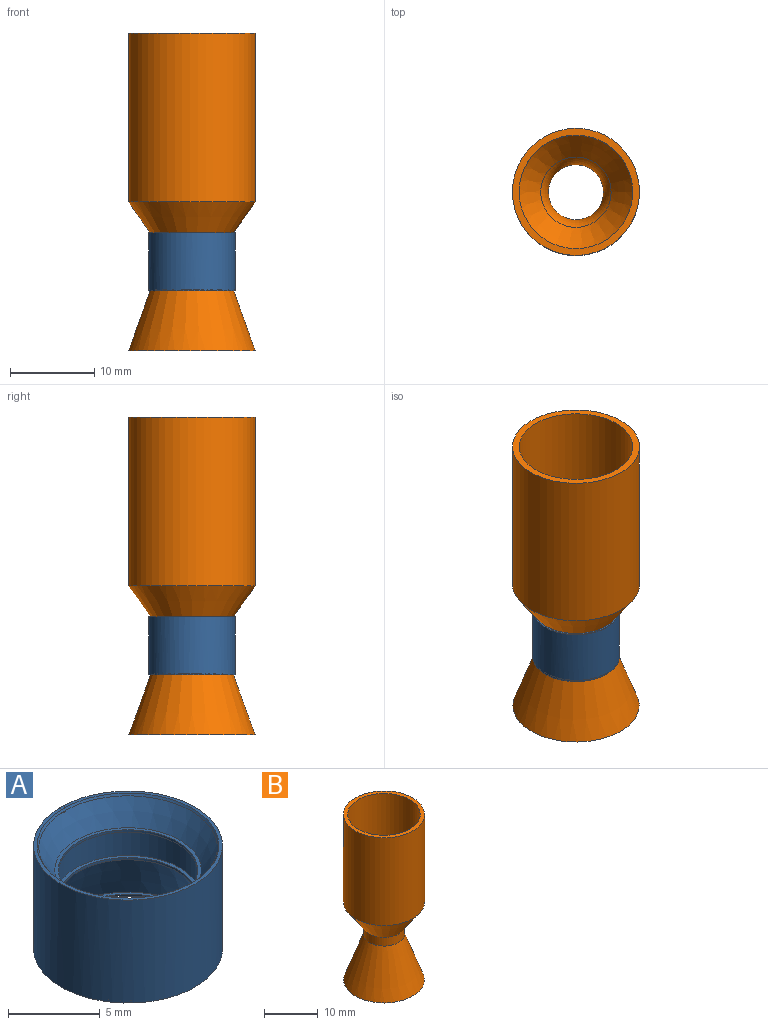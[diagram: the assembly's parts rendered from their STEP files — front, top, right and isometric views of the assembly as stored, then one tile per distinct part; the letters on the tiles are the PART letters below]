
ASSEMBLY  parts=2 mates=1
PART A: 31 faces, bbox 10.7x10.7x6.9 mm
  f0: cone r=4mm half-angle=35.2deg, axis (0,0,1), area 52.6mm2, adj f1,f10,f25,f26,f27
  f1: plane 10.13x10.13mm, normal (0,0,-1), area 6.2mm2, adj f0,f11,f25,f26,f27
  f2: plane 10.3x10.3mm, normal (0,0,1), area 6.2mm2, adj f11,f12,f22,f23,f24
  f3: plane 10.19x10.19mm, normal (0,0,1), area 6.2mm2, adj f4,f5,f14,f17,f18,f19
  f4: cone r=5.1mm half-angle=19.6deg, axis (0,0,-1), area 93.4mm2, adj f3,f5,f15,f17,f18,f19
  f5: cone r=5.1mm half-angle=19.6deg, axis (0,0,-1), area 0mm2, adj f3,f4,f19
  f6: plane 8x8mm, normal (0,0,1), area 4.9mm2, adj f7,f16
  f7: cylinder r=4mm len=8mm, axis (0,0,1), area 42.7mm2, adj f6,f8
  f8: plane 8x8mm, normal (0,0,-1), area 4.9mm2, adj f7,f9
  f9: cylinder r=3.8mm len=7.6mm, axis (0,0,1), area 3.6mm2, adj f8,f10
  f10: plane 8x8mm, normal (0,0,1), area 4.9mm2, adj f0,f9
  f11: cone r=4.95mm half-angle=35.2deg, axis (0,0,1), area 4.6mm2, adj f1,f2
  f12: cylinder r=5.15mm len=10.3mm, axis (0,0,1), area 222.2mm2, adj f2,f13,f21
  f13: plane 10.31x10.31mm, normal (0,0,-1), area 6.3mm2, adj f12,f14
  f14: cone r=4.95mm half-angle=19.6deg, axis (0,0,-1), area 4.9mm2, adj f3,f13
  f15: plane 8x8mm, normal (0,0,-1), area 4.9mm2, adj f4,f16
  f16: cylinder r=3.8mm len=7.6mm, axis (0,0,1), area 3.6mm2, adj f6,f15
  f17: plane 0.41x0.27mm, normal (0,-1,0), area 0.1mm2, adj f3,f4,f18,f19
  f18: plane 0.4x0.14mm, normal (1,0,0), area 0mm2, adj f3,f4,f17
  f19: plane 0.4x0.14mm, normal (-1,0,0), area 0mm2, adj f3,f4,f5,f17
  f20: plane 0.26x0.2mm, normal (0,0,1), area 0.1mm2, adj f21,f22,f23,f24
  f21: plane 0.26x0.01mm, normal (0,1,0), area 0mm2, adj f12,f20,f24
  f22: plane 0.26x0.01mm, normal (0,-1,0), area 0mm2, adj f2,f20,f23,f24
  f23: plane 0.2x0.01mm, normal (1,0,0), area 0mm2, adj f2,f20,f22
  f24: plane 0.19x0.01mm, normal (-1,0,0), area 0mm2, adj f2,f20,f21,f22
  f25: plane 0.15x0.11mm, normal (-1,0,0), area 0mm2, adj f0,f1,f27
  f26: plane 0.15x0.11mm, normal (1,0,0), area 0mm2, adj f0,f1,f27
  f27: plane 0.27x0.16mm, normal (0,-1,0), area 0mm2, adj f0,f1,f25,f26
  f28: torus R=4.57mm, axis (0,0,1), area 63.2mm2
  f29: torus R=4.57mm, axis (0,0,1), area 63.2mm2
  f30: torus R=4.57mm, axis (0,0,1), area 63.2mm2
PART B: 11 faces, bbox 23.6x23.6x41.8 mm
  f0: cone r=3.8mm half-angle=19.6deg, axis (0,0,-1), area 390.3mm2, adj f1,f8
  f1: plane 14.99x14.99mm, normal (0,0,-1), area 35.7mm2, adj f0,f2
  f2: cone r=3mm half-angle=19.6deg, axis (0,0,-1), area 236.9mm2, adj f1,f9
  f3: cone r=6.74mm half-angle=35.2deg, axis (0,0,1), area 153mm2, adj f4,f10
  f4: cylinder r=6.74mm len=20mm, axis (0,0,1), area 847.6mm2, adj f3,f5
  f5: plane 15.09x15.09mm, normal (0,0,1), area 35.9mm2, adj f4,f6
  f6: cylinder r=7.54mm len=20mm, axis (0,0,1), area 948.1mm2, adj f5,f7
  f7: cone r=7.54mm half-angle=35.2deg, axis (0,0,1), area 231.7mm2, adj f6,f8
  f8: cylinder r=3.8mm len=7.6mm, axis (0,0,1), area 47.8mm2, adj f0,f7
  f9: torus R=30.79mm, axis (0,0,1), area 94.1mm2, adj f2,f10
  f10: torus R=8.26mm, axis (0,0,-1), area 90mm2, adj f3,f9
PLACE A t=(0,0,-0.01)mm
PLACE B at identity
MATE fastened A.f0 <-> B.f0  axis (0,0,1) through (15.28,0,-6.31)mm
